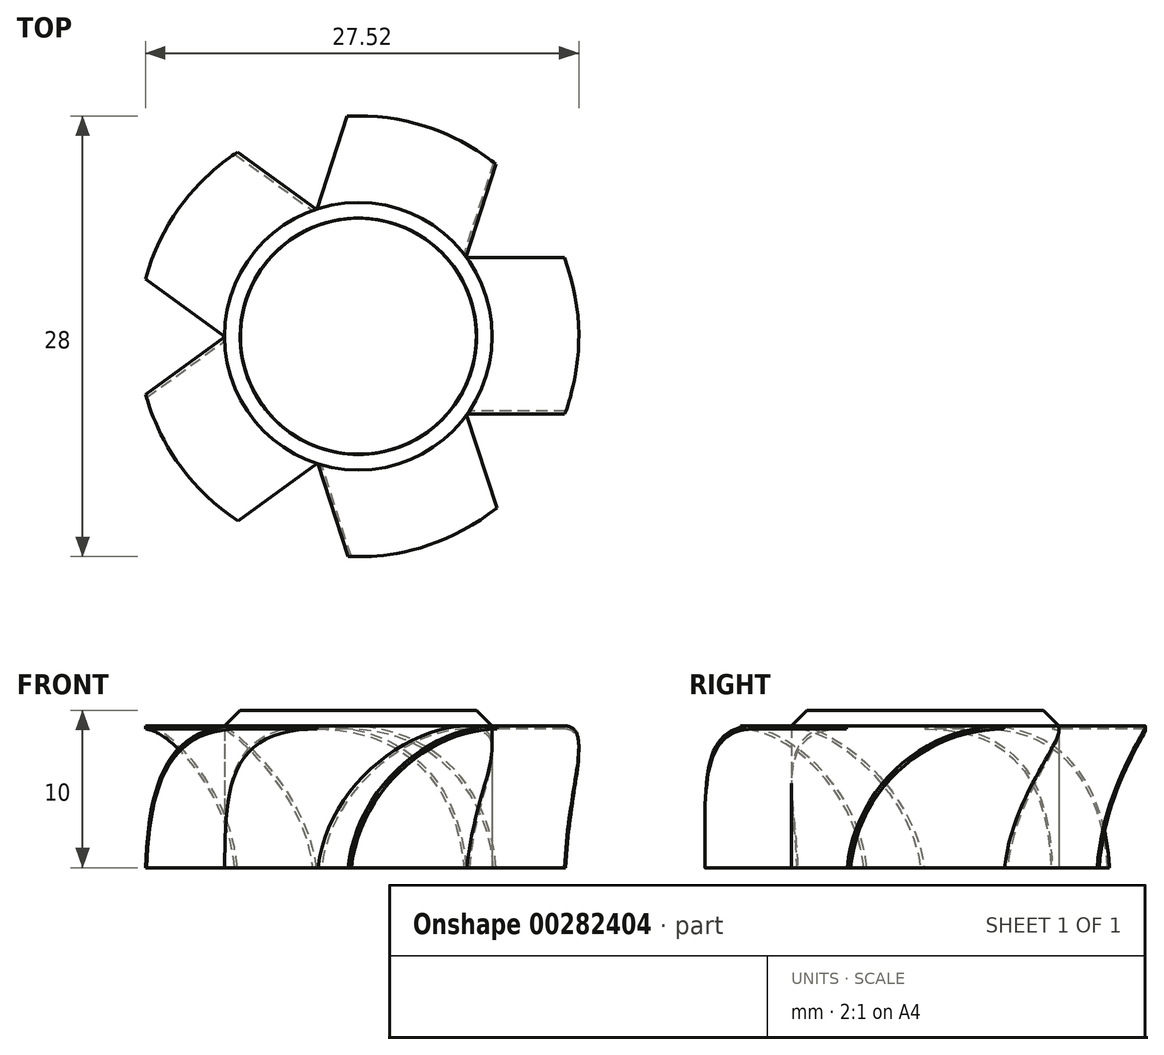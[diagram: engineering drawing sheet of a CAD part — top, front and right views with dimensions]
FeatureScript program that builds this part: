
annotation { "Feature Type Name" : "Feature", "Feature Type Description" : "" }
export const myFeature = defineFeature(function(context is Context, id is Id, definition is map)
    precondition{}
    {
        {
            var Q0;
            Q0=qCreatedBy(makeId("Top.planeOp"),FACE);
            var sketch = newSketch(context, id + "F0", { "sketchPlane" : qUnion([Q0])});
            skCircle(sketch, "E0", {"center": v(0, 0) * mm, "radius": 8.5 * mm});
            skSolve(sketch);
        }
        {
            var Q0;
            Q0=qSketchRegion(id+"F0",true);
            extrude(context, id + "F1", {"entities" : qUnion([Q0]), "depth" : 10 * mm});
        }
        {
            var Q0;
            Q0=makeQuery(id+"F1.opExtrude","CAP_EDGE",EDGE,{"disambiguationData":[OSD([sQuery(id+"F0.wireOp",EDGE,"E0")])],"isStart":false});
            chamfer(context, id + "F2", {"entities" : qUnion([Q0]), "width" : 1 * mm, "tangentPropagation" : true});
        }
        {
            var Q0;
            Q0=qCreatedBy(makeId("Right.planeOp"),FACE);
            var sketch = newSketch(context, id + "F3", { "sketchPlane" : qUnion([Q0])});
            skArc(sketch, "E1", {"start": v(5, 9) * mm, "mid": v(-1.7, 6.42) * mm, "end": v(-4.95, 0) * mm});
            skLineSegment(sketch, "E2", {"start": v(0, 9) * mm, "end": v(5, 9) * mm, "construction": true});
            skArc(sketch, "E3.0", {"start": v(5, 8.8) * mm, "mid": v(-1.57, 6.27) * mm, "end": v(-4.75, 0) * mm});
            skLineSegment(sketch, "E4", {"start": v(5, 8.8) * mm, "end": v(5, 9) * mm});
            skLineSegment(sketch, "E5", {"start": v(-4.95, 0) * mm, "end": v(-4.75, 0) * mm});
            skSolve(sketch);
        }
        {
            var Q0;
            Q0=qSketchRegion(id+"F3",true);
            extrude(context, id + "F4", {"entities" : qUnion([Q0]), "operationType" : NewBodyOperationType.ADD, "depth" : 25 * mm});
        }
        {
            var Q0;
            Q0=qCreatedBy(makeId("Right.planeOp"),FACE);
            var sketch = newSketch(context, id + "F5", { "sketchPlane" : qUnion([Q0])});
            skLineSegment(sketch, "E6", {"start": v(0, 0) * mm, "end": v(0, 16.86) * mm, "construction": true});
            skSolve(sketch);
        }
        {
            var Q0;
            Q0=makeQuery(id+"F1.opExtrude","SWEPT_BODY",BODY,{"disambiguationData":[OSD([sQuery(id+"F0.wireOp",EDGE,"E0")])]});
            var Q1;
            Q1=sQuery(id+"F5.wireOp",EDGE,"E6");
            circularPattern(context, id + "F6", {"entities" : qUnion([Q0]), "axis" : qUnion([Q1]), "angle" : 360 * degree, "instanceCount" : 5, "equalSpace" : true});
        }
        {
            var Q0;
            Q0=qCreatedBy(makeId("Top.planeOp"),FACE);
            var sketch = newSketch(context, id + "F7", { "sketchPlane" : qUnion([Q0])});
            skCircle(sketch, "E7", {"center": v(0, 0) * mm, "radius": 14 * mm});
            skCircle(sketch, "E8", {"center": v(0, 0) * mm, "radius": 30 * mm});
            skSolve(sketch);
        }
        {
            var Q0;
            Q0=qSketchRegion(id+"F7",true);
            extrude(context, id + "F8", {"entities" : qUnion([Q0]), "operationType" : NewBodyOperationType.REMOVE, "depth" : 25 * mm});
        }
    });
